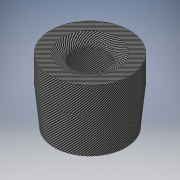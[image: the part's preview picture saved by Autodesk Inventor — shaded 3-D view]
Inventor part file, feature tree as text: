
AUTODESK INVENTOR PART (.ipt)
format: ipt  version: 2017 SP1 (Build 210196100, 196)  size: 173,568 bytes
history: native  units: in
note: dims shown in document units (in); Inventor stores cm internally (conversion verified against a paired STEP export)
features: revolve x1, sketch x1
ambient origin geometry x8: Origin, YZ Plane, XZ Plane, XY Plane, X Axis, Y Axis, Z Axis, Center Point
bodies: Solid1 (feature_tree)
feature tree (2):
  revolve  "Revolution1"  [1 undecoded]
  sketch  "Sketch1"  dims[d0=0.5in d1=1.13in d3=15.0deg d4=0.25in d9=1.5in d11=0.5in d13=3.75in d14=0.25in d15=1.0in d16=0.25in d17=0.5in d18=0.234in d19=0.234in d20=0.5in d22=4.25in d23=2.5in d25=1.0in d26=0.25in d27=5.25in d28=0.125in d29=4.0in d30=0.25in d31=0.1718in d32=1.75in d33=0.125in d34=0.801in d35=0.375in d37=90.0deg]
note: 1 required parameter value undecoded (feature->parameter linkage not recoverable at this tier; creation-order binding heuristic only, values carry confidence <= 0.55)
